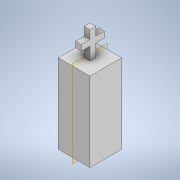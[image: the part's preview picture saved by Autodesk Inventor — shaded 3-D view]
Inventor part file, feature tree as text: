
AUTODESK INVENTOR PART (.ipt)
format: ipt  version: 2021 (Build 250183000, 183)  size: 119,808 bytes
history: native  units: in
note: dims shown in document units (in); Inventor stores cm internally (conversion verified against a paired STEP export)
features: extrude x2, sketch x2, plane x1
ambient origin geometry x8: Origin, YZ Plane, XZ Plane, XY Plane, X Axis, Y Axis, Z Axis, Center Point
bodies: Solid1 (feature_tree)
feature tree (5):
  extrude  "Extrusion1"  Depth=0.8661in
  plane  "Work Plane1"
  extrude  "Extrusion2"  Depth=0.1575in
  sketch  "Sketch1"  dims[d0=0.8661in d1=0.8661in]
  sketch  "Sketch2"  dims[d2=2.1654in d3=0.0in d4=0.0787in d5=0.3543in d6=0.2362in d7=0.1575in d8=0.2362in d9=0.1575in d10=0.2362in d11=0.1575in d12=0.0in]
